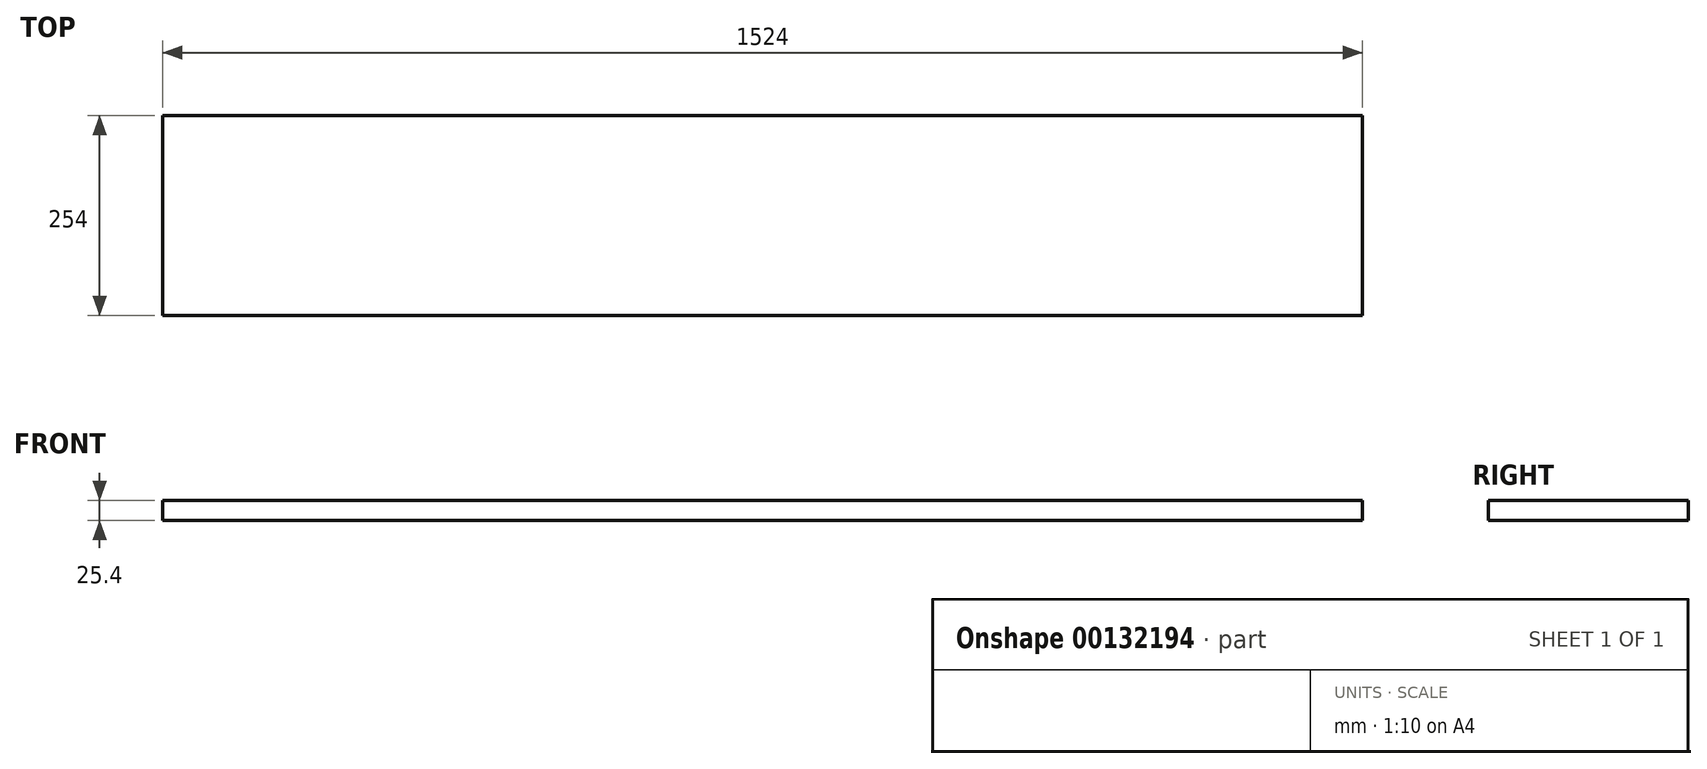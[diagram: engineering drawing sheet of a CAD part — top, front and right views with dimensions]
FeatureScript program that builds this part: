
annotation { "Feature Type Name" : "Feature", "Feature Type Description" : "" }
export const myFeature = defineFeature(function(context is Context, id is Id, definition is map)
    precondition{}
    {
        {
            var Q0;
            Q0=qCreatedBy(makeId("Top.planeOp"),FACE);
            var sketch = newSketch(context, id + "F0", { "sketchPlane" : qUnion([Q0])});
            skLineSegment(sketch, "E0.bottom", {"start": v(0, 0) * mm, "end": v(1524, 0) * mm});
            skLineSegment(sketch, "E0.top", {"start": v(0, 254) * mm, "end": v(1524, 254) * mm});
            skLineSegment(sketch, "E0.left", {"start": v(0, 0) * mm, "end": v(0, 254) * mm});
            skLineSegment(sketch, "E0.right", {"start": v(1524, 0) * mm, "end": v(1524, 254) * mm});
            skSolve(sketch);
        }
        {
            var Q0;
            Q0 = qSketchRegion(id + "F0", true);
            extrude(context, id + "F1", {"entities" : qUnion([Q0]), "depth" : 25.4 * mm});
        }
    });
